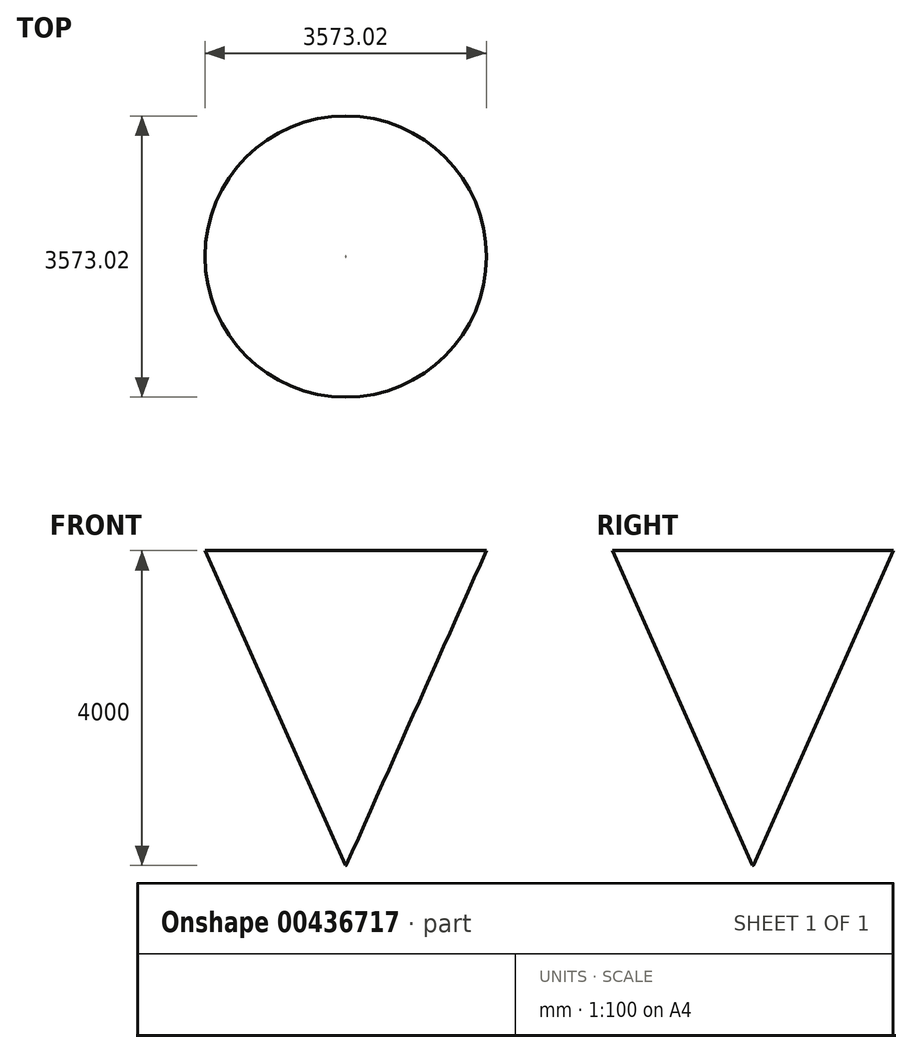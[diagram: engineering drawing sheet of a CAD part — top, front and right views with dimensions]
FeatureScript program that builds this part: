
annotation { "Feature Type Name" : "Feature", "Feature Type Description" : "" }
export const myFeature = defineFeature(function(context is Context, id is Id, definition is map)
    precondition{}
    {
        {
            var Q0;
            Q0=qCreatedBy(makeId("Top.planeOp"),FACE);
            var sketch = newSketch(context, id + "F0", { "sketchPlane" : qUnion([Q0])});
            skCircle(sketch, "E0", {"center": v(0, 0) * mm, "radius": 5.6 * mm});
            skSolve(sketch);
        }
        {
            var Q0;
            Q0=makeQuery(id+"F0.imprint","IMPRINT",FACE,{"disambiguationData":[TD([[makeQuery(id+"F0.imprint","IMPRINT",EDGE,{"derivedFrom":sQuery(id+"F0.wireOp",EDGE,"E0")}),1.0]])]});
            extrude(context, id + "F1", {"entities" : qUnion([Q0]), "depth" : 4000 * mm, "hasDraft" : true, "draftAngle" : 24 * degree});
        }
    });
